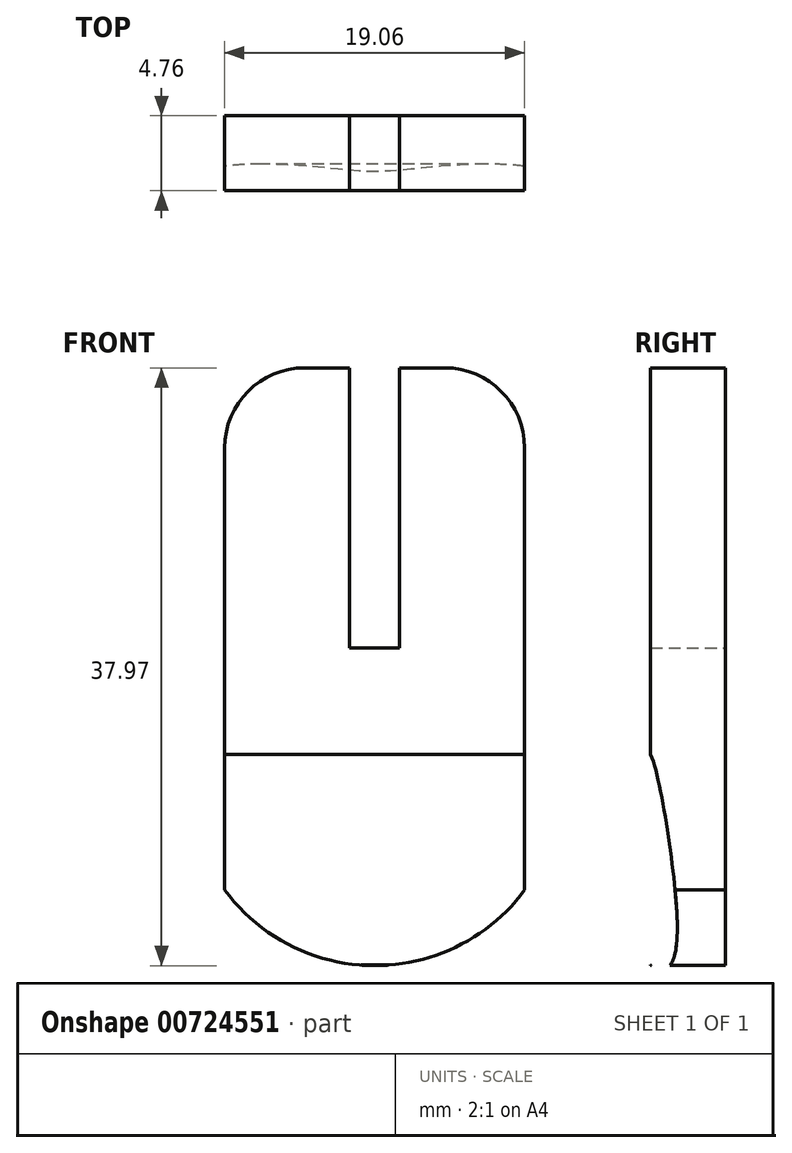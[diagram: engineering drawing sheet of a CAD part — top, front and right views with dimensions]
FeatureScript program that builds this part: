
annotation { "Feature Type Name" : "Feature", "Feature Type Description" : "" }
export const myFeature = defineFeature(function(context is Context, id is Id, definition is map)
    precondition{}
    {
        {
            var Q0;
            Q0=qCreatedBy(makeId("Front.planeOp"),FACE);
            var sketch = newSketch(context, id + "F0", { "sketchPlane" : qUnion([Q0])});
            skLineSegment(sketch, "E0.bottom", {"start": v(9.53, -19.05) * mm, "end": v(-9.53, -19.05) * mm});
            skLineSegment(sketch, "E0.top", {"start": v(9.52, 19.05) * mm, "end": v(-9.52, 19.05) * mm});
            skLineSegment(sketch, "E0.left", {"start": v(9.52, -19.05) * mm, "end": v(9.53, 19.05) * mm});
            skLineSegment(sketch, "E0.right", {"start": v(-9.53, -19.05) * mm, "end": v(-9.52, 19.05) * mm});
            skPoint(sketch, "E0.middle", {"position": v(0, 0) * mm});
            skLineSegment(sketch, "E1.bottom", {"start": v(1.59, 1.27) * mm, "end": v(-1.59, 1.27) * mm});
            skLineSegment(sketch, "E1.top", {"start": v(1.59, 36.83) * mm, "end": v(-1.59, 36.83) * mm});
            skLineSegment(sketch, "E1.left", {"start": v(1.59, 1.27) * mm, "end": v(1.59, 36.83) * mm});
            skLineSegment(sketch, "E1.right", {"start": v(-1.59, 1.27) * mm, "end": v(-1.59, 36.83) * mm});
            skPoint(sketch, "E1.middle", {"position": v(0, 19.05) * mm});
            skSolve(sketch);
        }
        {
            var Q0;
            Q0=makeQuery(id+"F0.imprint","IMPRINT",FACE,{"disambiguationData":[TD([[makeQuery(id+"F0.imprint","IMPRINT",EDGE,{"derivedFrom":sQuery(id+"F0.wireOp",EDGE,"E0.bottom")}),-1.0]])]});
            extrude(context, id + "F1", {"entities" : qUnion([Q0]), "depth" : 4.76 * mm, "offsetDistance" : 25.4 * mm});
        }
        {
            var Q0;
            Q0=makeQuery(id+"F1.opExtrude","CAP_FACE",FACE,{"disambiguationData":[OSD([sQuery(id+"F0.wireOp",EDGE,"E0.bottom"),sQuery(id+"F0.wireOp",EDGE,"E0.top"),sQuery(id+"F0.wireOp",EDGE,"E0.left"),sQuery(id+"F0.wireOp",EDGE,"E0.right"),sQuery(id+"F0.wireOp",EDGE,"E1.bottom"),sQuery(id+"F0.wireOp",EDGE,"E1.left"),sQuery(id+"F0.wireOp",EDGE,"E1.right")])],"isStart":false});
            var sketch = newSketch(context, id + "F2", { "sketchPlane" : qUnion([Q0])});
            skArc(sketch, "E2", {"start": v(-9.53, 0) * mm, "mid": v(0, -18.91) * mm, "end": v(9.53, 0) * mm});
            skArc(sketch, "E3", {"start": v(-9.53, 0) * mm, "mid": v(0, -27.52) * mm, "end": v(9.53, 0) * mm});
            skSolve(sketch);
        }
        {
            var Q0;
            Q0 = qSketchRegion(id + "F2", true);
            extrude(context, id + "F3", {"entities" : qUnion([Q0]), "operationType" : NewBodyOperationType.REMOVE, "oppositeDirection" : true, "depth" : 25.4 * mm, "offsetDistance" : 25.4 * mm});
        }
        {
            var Q0;
            Q0=makeQuery(id+"F1.opExtrude","SWEPT_EDGE",EDGE,{"disambiguationData":[OSD([sQuery(id+"F0.wireOp",EDGE,"E0.top"),sQuery(id+"F0.wireOp",EDGE,"E0.left")])]});
            var Q1;
            Q1=makeQuery(id+"F1.opExtrude","SWEPT_EDGE",EDGE,{"disambiguationData":[OSD([sQuery(id+"F0.wireOp",EDGE,"E0.top"),sQuery(id+"F0.wireOp",EDGE,"E0.right")])]});
            fillet(context, id + "F4", {"entities" : qUnion([Q0, Q1]), "radius" : 5.08 * mm, "tangentPropagation" : true, "allowEdgeOverflow" : false});
        }
        {
            var Q0;
            Q0=makeQuery(id+"F1.opExtrude","SWEPT_FACE",FACE,{"disambiguationData":[OSD([sQuery(id+"F0.wireOp",EDGE,"E0.right")])]});
            var sketch = newSketch(context, id + "F5", { "sketchPlane" : qUnion([Q0])});
            skFitSpline(sketch, "E4", {"points": [v(3.68, -19.04) * mm, v(3.54, -11.43) * mm, v(5.31, -5.05) * mm, v(5.9, -17.07) * mm, v(3.68, -19.04) * mm]});
            skSolve(sketch);
        }
        {
            var Q0;
            Q0 = qSketchRegion(id + "F5", true);
            extrude(context, id + "F6", {"entities" : qUnion([Q0]), "operationType" : NewBodyOperationType.REMOVE, "oppositeDirection" : true, "depth" : 25.4 * mm, "offsetDistance" : 25.4 * mm});
        }
    });
